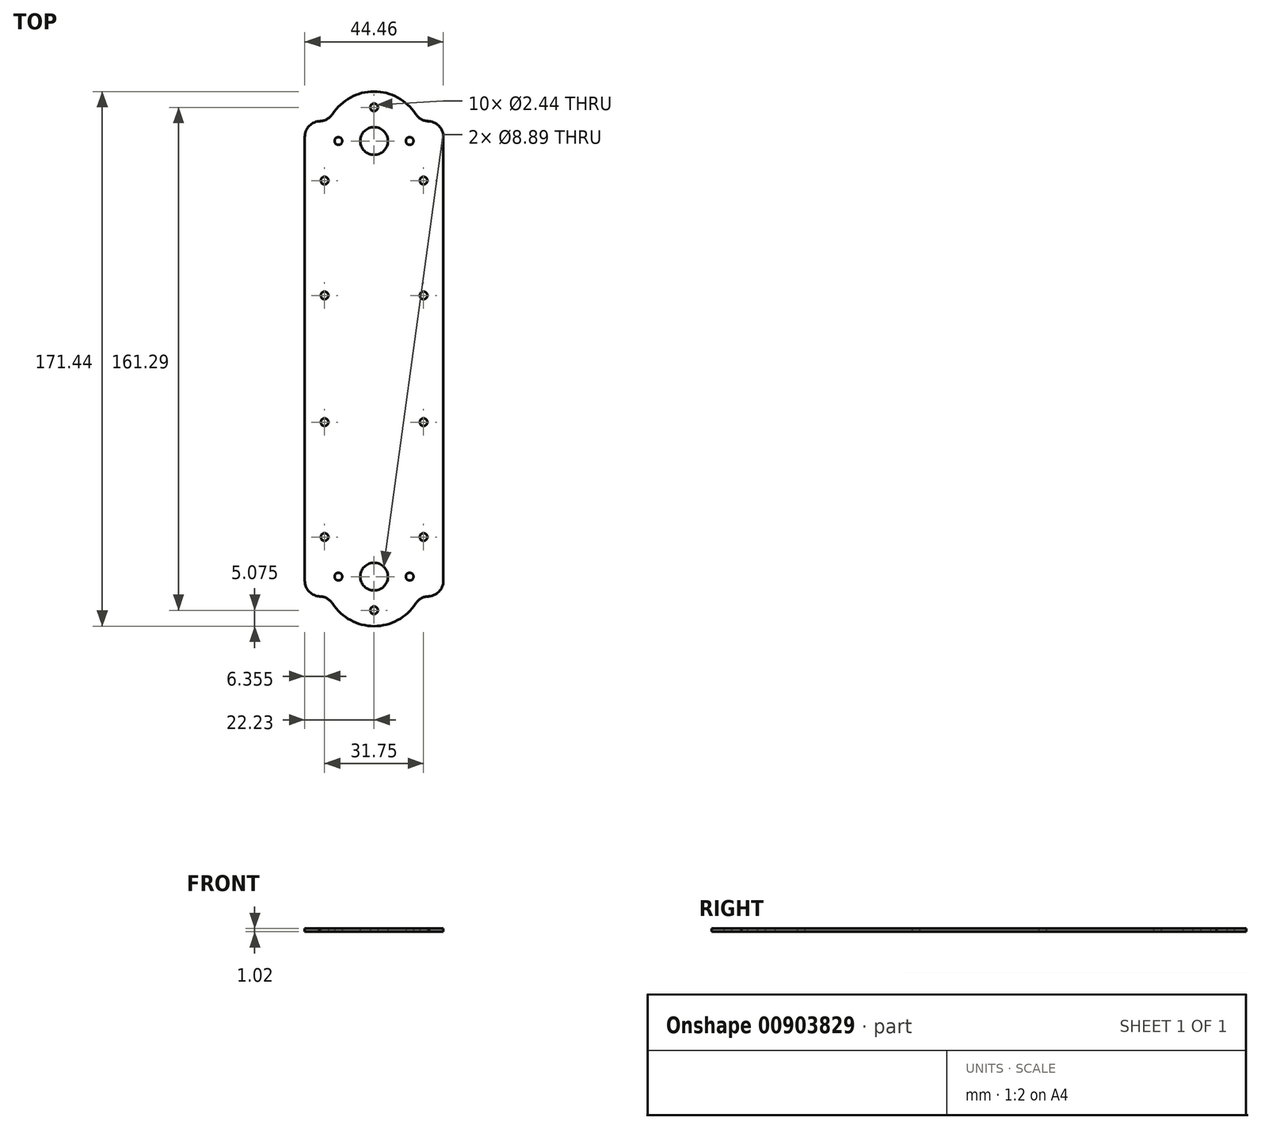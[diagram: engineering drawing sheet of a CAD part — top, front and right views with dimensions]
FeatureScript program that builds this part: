
annotation { "Feature Type Name" : "Feature", "Feature Type Description" : "" }
export const myFeature = defineFeature(function(context is Context, id is Id, definition is map)
    precondition{}
    {
        {
            var Q0;
            Q0=qCreatedBy(makeId("Top.planeOp"),FACE);
            var sketch = newSketch(context, id + "F0", { "sketchPlane" : qUnion([Q0])});
            skLineSegment(sketch, "E0.bottom", {"start": v(17.56, -76.2) * mm, "end": v(17.15, -76.2) * mm});
            skLineSegment(sketch, "E0.top", {"start": v(17.56, 76.2) * mm, "end": v(17.14, 76.2) * mm});
            skLineSegment(sketch, "E0.left", {"start": v(22.23, -71.12) * mm, "end": v(22.22, 71.12) * mm});
            skLineSegment(sketch, "E0.right", {"start": v(-22.23, -71.12) * mm, "end": v(-22.23, 71.12) * mm});
            skPoint(sketch, "E0.middle", {"position": v(0, 0) * mm});
            skLineSegment(sketch, "E1", {"start": v(0, 0) * mm, "end": v(0, 69.85) * mm, "construction": true});
            skLineSegment(sketch, "E2", {"start": v(0, 0) * mm, "end": v(0, -69.85) * mm, "construction": true});
            skPoint(sketch, "E2.endSnap0", {"position": v(0, -76.2) * mm});
            skCircle(sketch, "E3", {"center": v(0, 69.85) * mm, "radius": 4.45 * mm});
            skCircle(sketch, "E4", {"center": v(0, -69.85) * mm, "radius": 4.45 * mm});
            skArc(sketch, "E5.0", {"start": v(13.3, 78.5) * mm, "mid": v(0, 85.73) * mm, "end": v(-13.3, 78.5) * mm});
            skArc(sketch, "E6.0", {"start": v(-13.3, -78.5) * mm, "mid": v(0, -85.73) * mm, "end": v(13.3, -78.5) * mm});
            skLineSegment(sketch, "E7.trimOffspring", {"start": v(-17.15, 76.2) * mm, "end": v(-17.56, 76.2) * mm});
            skLineSegment(sketch, "E8.trimOffspring", {"start": v(-17.14, -76.2) * mm, "end": v(-17.56, -76.2) * mm});
            skPoint(sketch, "E9.visualSharp", {"position": v(-22.23, 76.2) * mm});
            skArc(sketch, "E9.filletArc", {"start": v(-17.15, 76.2) * mm, "mid": v(-20.74, 74.71) * mm, "end": v(-22.23, 71.12) * mm});
            skPoint(sketch, "E10.visualSharp", {"position": v(22.22, 76.2) * mm});
            skArc(sketch, "E10.filletArc", {"start": v(22.22, 71.12) * mm, "mid": v(20.74, 74.71) * mm, "end": v(17.14, 76.2) * mm});
            skPoint(sketch, "E11.visualSharp", {"position": v(22.23, -76.2) * mm});
            skArc(sketch, "E11.filletArc", {"start": v(17.15, -76.2) * mm, "mid": v(20.74, -74.71) * mm, "end": v(22.23, -71.12) * mm});
            skPoint(sketch, "E12.visualSharp", {"position": v(-22.23, -76.2) * mm});
            skArc(sketch, "E12.filletArc", {"start": v(-22.23, -71.12) * mm, "mid": v(-20.74, -74.71) * mm, "end": v(-17.14, -76.2) * mm});
            skPoint(sketch, "E13.visualSharp", {"position": v(-14.55, 76.2) * mm});
            skArc(sketch, "E13.filletArc", {"start": v(-17.56, 76.2) * mm, "mid": v(-15.14, 76.81) * mm, "end": v(-13.3, 78.5) * mm});
            skPoint(sketch, "E14.visualSharp", {"position": v(14.55, 76.2) * mm});
            skArc(sketch, "E14.filletArc", {"start": v(13.3, 78.5) * mm, "mid": v(15.14, 76.81) * mm, "end": v(17.56, 76.2) * mm});
            skPoint(sketch, "E15.visualSharp", {"position": v(-14.55, -76.2) * mm});
            skArc(sketch, "E15.filletArc", {"start": v(-13.3, -78.5) * mm, "mid": v(-15.14, -76.81) * mm, "end": v(-17.56, -76.2) * mm});
            skPoint(sketch, "E16.visualSharp", {"position": v(14.55, -76.2) * mm});
            skArc(sketch, "E16.filletArc", {"start": v(17.56, -76.2) * mm, "mid": v(15.14, -76.81) * mm, "end": v(13.3, -78.5) * mm});
            skLineSegment(sketch, "E17", {"start": v(0, 69.85) * mm, "end": v(11.43, 69.85) * mm, "construction": true});
            skLineSegment(sketch, "E18", {"start": v(0, 69.85) * mm, "end": v(-11.43, 69.85) * mm, "construction": true});
            skCircle(sketch, "E19", {"center": v(-11.43, 69.85) * mm, "radius": 1.24 * mm});
            skCircle(sketch, "E20", {"center": v(11.43, 69.85) * mm, "radius": 1.24 * mm});
            skCircle(sketch, "E21.MirrorC", {"center": v(11.43, -69.85) * mm, "radius": 1.24 * mm});
            skCircle(sketch, "E22.MirrorC", {"center": v(-11.43, -69.85) * mm, "radius": 1.24 * mm});
            skCircle(sketch, "E23", {"center": v(-15.88, 57.15) * mm, "radius": 1.22 * mm});
            skCircle(sketch, "E24.1.0.0", {"center": v(-15.88, 20.32) * mm, "radius": 1.22 * mm});
            skLineSegment(sketch, "E24.direction1", {"start": v(-15.88, 57.15) * mm, "end": v(-15.88, 20.32) * mm, "construction": true});
            skCircle(sketch, "E25.MirrorC", {"center": v(15.88, 57.15) * mm, "radius": 1.22 * mm});
            skCircle(sketch, "E26.MirrorC", {"center": v(15.88, 20.32) * mm, "radius": 1.22 * mm});
            skCircle(sketch, "E27.MirrorC", {"center": v(-15.88, -57.15) * mm, "radius": 1.22 * mm});
            skCircle(sketch, "E28.MirrorC", {"center": v(-15.88, -20.32) * mm, "radius": 1.22 * mm});
            skCircle(sketch, "E29.MirrorC", {"center": v(15.88, -20.32) * mm, "radius": 1.22 * mm});
            skCircle(sketch, "E30.MirrorC", {"center": v(15.88, -57.15) * mm, "radius": 1.22 * mm});
            skLineSegment(sketch, "E31", {"start": v(0, 69.85) * mm, "end": v(0, 80.65) * mm, "construction": true});
            skCircle(sketch, "E32", {"center": v(0, 80.65) * mm, "radius": 1.22 * mm});
            skCircle(sketch, "E33.MirrorC", {"center": v(0, -80.65) * mm, "radius": 1.22 * mm});
            skSolve(sketch);
        }
        {
            var Q0;
            Q0 = qSketchRegion(id + "F0", true);
            extrude(context, id + "F1", {"entities" : qUnion([Q0]), "depth" : 1.02 * mm, "offsetDistance" : 25.4 * mm});
        }
    });
